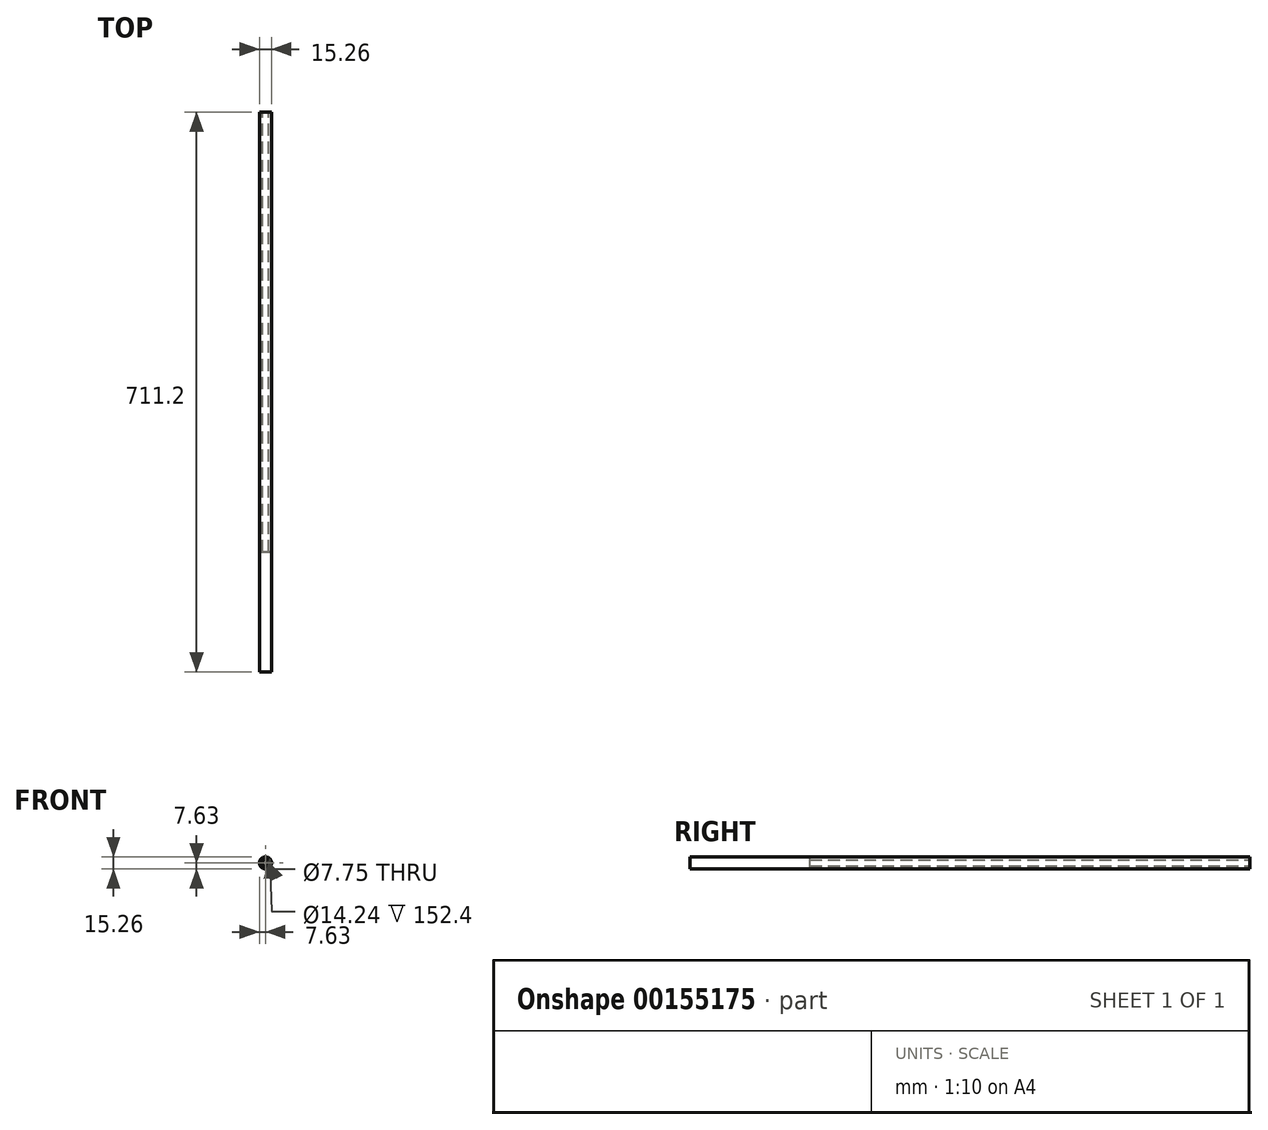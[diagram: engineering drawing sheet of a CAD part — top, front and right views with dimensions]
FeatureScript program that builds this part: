
annotation { "Feature Type Name" : "Feature", "Feature Type Description" : "" }
export const myFeature = defineFeature(function(context is Context, id is Id, definition is map)
    precondition{}
    {
        {
            var Q0;
            Q0=qCreatedBy(makeId("Front.planeOp"),FACE);
            var sketch = newSketch(context, id + "F0", { "sketchPlane" : qUnion([Q0])});
            skCircle(sketch, "E0", {"center": v(0, 0) * mm, "radius": 3.87 * mm});
            skCircle(sketch, "E1", {"center": v(0, 0) * mm, "radius": 7.63 * mm});
            skSolve(sketch);
        }
        {
            var Q0;
            Q0=makeQuery(id+"F0.imprint","IMPRINT",FACE,{"disambiguationData":[TD([[makeQuery(id+"F0.imprint","IMPRINT",EDGE,{"derivedFrom":sQuery(id+"F0.wireOp",EDGE,"E0")}),-1.0]])]});
            extrude(context, id + "F1", {"entities" : qUnion([Q0]), "depth" : 558.8 * mm});
        }
        {
            var Q0;
            Q0=qCreatedBy(makeId("Front.planeOp"),FACE);
            var sketch = newSketch(context, id + "F2", { "sketchPlane" : qUnion([Q0])});
            skCircle(sketch, "E2.0", {"center": v(0, 0) * mm, "radius": 7.63 * mm});
            skCircle(sketch, "E3", {"center": v(0, 0) * mm, "radius": 7.12 * mm});
            skSolve(sketch);
        }
        {
            var Q0;
            Q0=makeQuery(id+"F1.opExtrude","CAP_FACE",FACE,{"disambiguationData":[OSD([sQuery(id+"F0.wireOp",EDGE,"E0"),sQuery(id+"F0.wireOp",EDGE,"E1")])],"isStart":false});
            var sketch = newSketch(context, id + "F3", { "sketchPlane" : qUnion([Q0])});
            skCircle(sketch, "E4.0", {"center": v(0, 0) * mm, "radius": 7.12 * mm});
            skCircle(sketch, "E5.0", {"center": v(0, 0) * mm, "radius": 7.63 * mm});
            skSolve(sketch);
        }
        {
            var Q0;
            Q0=makeQuery(id+"F3.imprint","IMPRINT",FACE,{"disambiguationData":[TD([[makeQuery(id+"F3.imprint","IMPRINT",EDGE,{"derivedFrom":sQuery(id+"F3.wireOp",EDGE,"E4.0")}),-1.0]])]});
            extrude(context, id + "F4", {"entities" : qUnion([Q0]), "operationType" : NewBodyOperationType.ADD, "depth" : 152.4 * mm});
        }
    });
